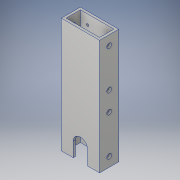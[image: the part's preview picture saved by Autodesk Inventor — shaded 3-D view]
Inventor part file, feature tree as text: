
AUTODESK INVENTOR PART (.ipt)
format: ipt  version: 2017 (Build 210142000, 142)  size: 162,304 bytes
history: native  units: in
note: dims shown in document units (in); Inventor stores cm internally (conversion verified against a paired STEP export)
features: sketch x4, hole x3, extrude x2
ambient origin geometry x8: Origin, YZ Plane, XZ Plane, XY Plane, X Axis, Y Axis, Z Axis, Center Point
bodies: Solid1 (feature_tree)
feature tree (9):
  extrude  "Extrusion1"  Depth=1.0in
  hole  "Hole2"  [1 undecoded]
  hole  "Hole3"  [1 undecoded]
  sketch  "Sketch4"  dims[d6=6.0in d7=0.0in d8=0.25in d9=0.5in d10=0.25in d11=0.5in d19=0.25in d20=0.75in d21=0.375in d22=0.25in d23=0.5635in d24=1.0in d25=0.8108in d27=0.5in d28=0.5in d30=0.125in d31=1.0in d32=0.125in d33=0.75in d34=0.375in d35=0.25in d36=0.5635in d37=0.125in d38=0.8108in d39=0.625in d40=0.625in d41=0.75in d42=0.75in d43=0.375in d44=0.25in d45=0.5635in d46=1.0in d47=0.8108in d48=0.75in d49=0.75in d50=1.0in d51=0.0in]
  hole  "Hole4"  [1 undecoded]
  extrude  "Extrusion2"  Depth=0.5in
  sketch  "Sketch1"  dims[d0=2.0in d1=1.0in]
  sketch  "Sketch2"  dims[d2=1.75in d3=0.75in]
  sketch  "Sketch3"  dims[d4=0.125in d5=0.125in]
note: 3 required parameter values undecoded (feature->parameter linkage not recoverable at this tier; creation-order binding heuristic only, values carry confidence <= 0.55)
